# Revit family: Domotics-NetworkCabling-GEWISS-CABINETS_WALL-MOUNTED_10_6U
name_source: partatom
category: Apparecchi elettrici
units: mm (PartAtom-declared; Revit-internal decimal feet)

## family parameters
Condiviso = No
Host = Superficie
Mantenere orientamento annotazione = Sì
Punto di calcolo locali = Sì
Quota connettore circolare = Usa diametro
Taglio con vuoti quando caricato = No
Tipo di parte = Normale

## types (1)
- GW38432 - WALL CABINET 10 8U DEPTH 265MM
    Cabling unity = 8U
    Catalogue = DOMOTICS
    Category = 10â€ wall-mount cabinet
    Colour = Grey (RAL 7035)
    Descrizione = WALL CABINET 10 8U DEPTH 265MM
    Door opening = 180°
    Electrocod = 3752
    Finishing = Textured
    IDF = 9c3b2a50-5590-4e52-9c8f-468d1bdaf3f7
    IDT = 6908dd95ba2d4d7d80b407934de9d0a7
    IP degree = IP20
    Immagine tipo = A.jpg
    Material = Steel
    Modello = GW38432
    No. uprights = 2
    Outer dim. LxHxD (mm) = 325x400x262
    Produttore = GEWISS S.p.A.
    Prospetto di default = 1219 mm
    SEO = Board
    Static load capacity = 15KG
    Technical sheet = https://www.gewiss.com
    Type of door = Reversible
    URL = https://www.gewiss.com
    Version file RFA = 21.2

## geometry (parser evidence)
native form markers: Sweep x3
no freeform markers — native parametric forms only
